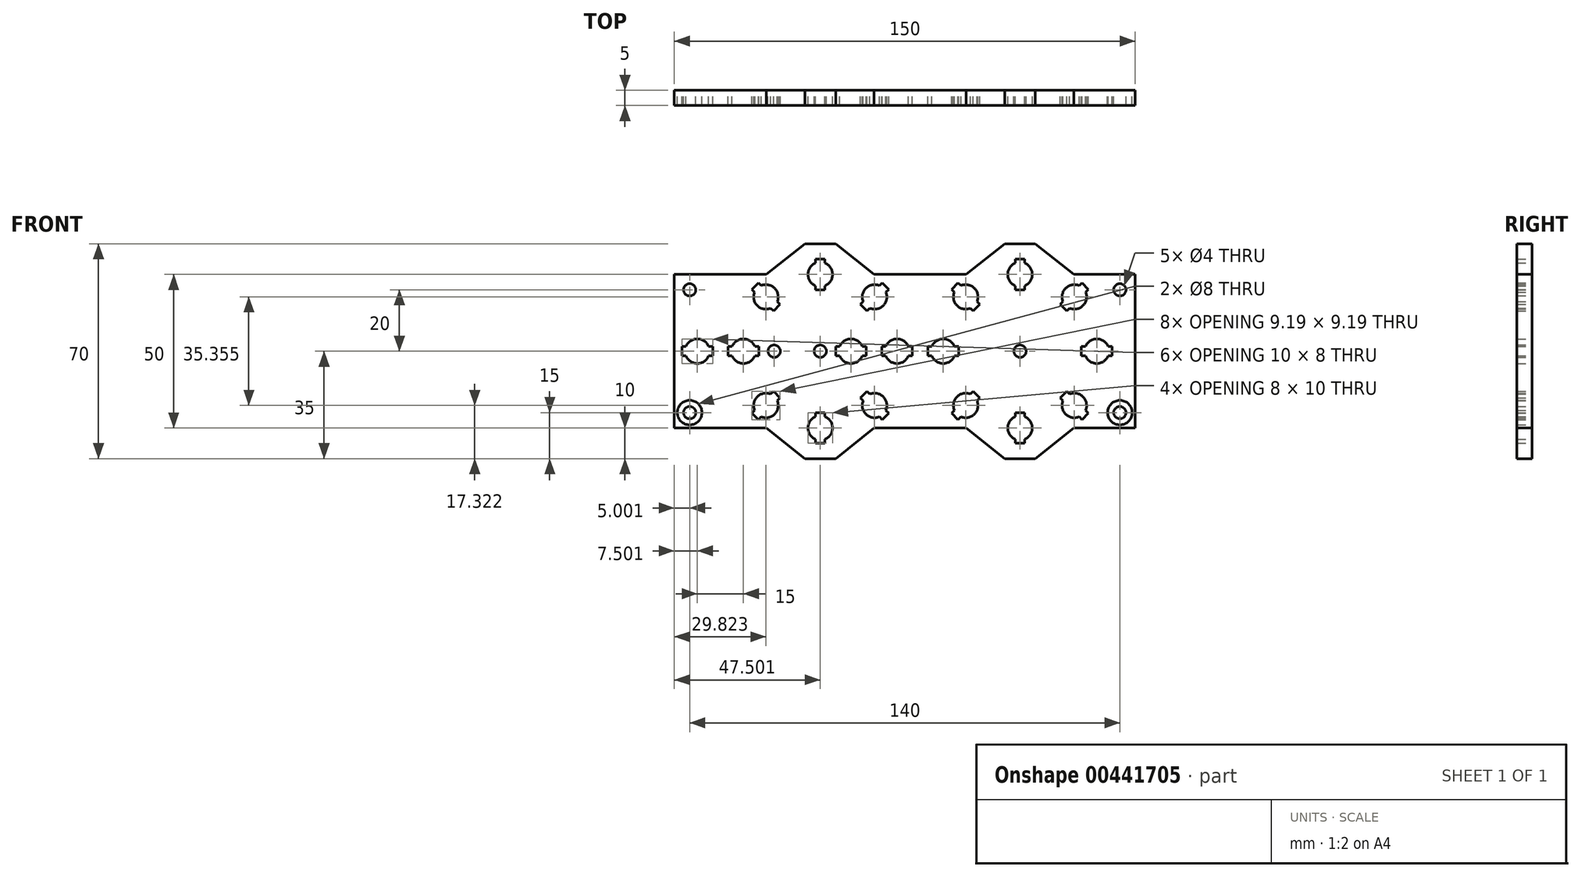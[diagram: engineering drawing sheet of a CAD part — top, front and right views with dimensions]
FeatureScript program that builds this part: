
annotation { "Feature Type Name" : "Feature", "Feature Type Description" : "" }
export const myFeature = defineFeature(function(context is Context, id is Id, definition is map)
    precondition{}
    {
        {
            var Q0;
            Q0=qCreatedBy(makeId("Front.planeOp"),FACE);
            var sketch = newSketch(context, id + "F0", { "sketchPlane" : qUnion([Q0])});
            skLineSegment(sketch, "E0", {"start": v(-68.18, 0) * mm, "end": v(-68.18, 25) * mm});
            skLineSegment(sketch, "E1", {"start": v(-68.18, 25) * mm, "end": v(-38.18, 25) * mm});
            skLineSegment(sketch, "E2", {"start": v(-38.18, 25) * mm, "end": v(-25.68, 35) * mm});
            skLineSegment(sketch, "E3", {"start": v(-25.68, 35) * mm, "end": v(-15.68, 35) * mm});
            skLineSegment(sketch, "E4", {"start": v(-15.68, 35) * mm, "end": v(-3.18, 25) * mm});
            skLineSegment(sketch, "E5", {"start": v(-3.18, 25) * mm, "end": v(26.82, 25) * mm});
            skLineSegment(sketch, "E6", {"start": v(26.82, 25) * mm, "end": v(39.32, 35) * mm});
            skLineSegment(sketch, "E7", {"start": v(39.32, 35) * mm, "end": v(49.32, 35) * mm});
            skLineSegment(sketch, "E8", {"start": v(49.32, 35) * mm, "end": v(61.82, 25) * mm});
            skLineSegment(sketch, "E9", {"start": v(61.82, 25) * mm, "end": v(81.82, 25) * mm});
            skLineSegment(sketch, "E10", {"start": v(81.82, 25) * mm, "end": v(81.82, 0) * mm});
            skLineSegment(sketch, "E11", {"start": v(-20.68, 68.45) * mm, "end": v(-20.68, -69.21) * mm, "construction": true});
            skLineSegment(sketch, "E12", {"start": v(44.32, 67.89) * mm, "end": v(44.32, -61.73) * mm, "construction": true});
            skLineSegment(sketch, "E13", {"start": v(87.46, 0) * mm, "end": v(-83.25, 0) * mm, "construction": true});
            skCircle(sketch, "E14", {"center": v(-20.68, 25) * mm, "radius": 4 * mm});
            skCircle(sketch, "E15", {"center": v(-20.68, 0) * mm, "radius": 25 * mm, "construction": true});
            skLineSegment(sketch, "E16", {"start": v(11.82, 59.27) * mm, "end": v(11.82, -51.7) * mm, "construction": true});
            skCircle(sketch, "E17.MirrorC", {"center": v(44.32, 0) * mm, "radius": 25 * mm, "construction": true});
            skCircle(sketch, "E18.MirrorC", {"center": v(44.32, 25) * mm, "radius": 4 * mm});
            skCircle(sketch, "E19.1.0", {"center": v(-38.36, 17.68) * mm, "radius": 4 * mm});
            skCircle(sketch, "E19.2.0", {"center": v(-45.68, 0) * mm, "radius": 4 * mm});
            skCircle(sketch, "E19.3.0", {"center": v(-38.36, -17.68) * mm, "radius": 4 * mm});
            skCircle(sketch, "E19.4.0", {"center": v(-20.68, -25) * mm, "radius": 4 * mm});
            skCircle(sketch, "E19.5.0", {"center": v(-3, -17.68) * mm, "radius": 4 * mm});
            skCircle(sketch, "E19.6.0", {"center": v(4.32, 0) * mm, "radius": 4 * mm});
            skCircle(sketch, "E19.7.0", {"center": v(-3, 17.68) * mm, "radius": 4 * mm});
            skCircle(sketch, "E20.MirrorC", {"center": v(62, 17.68) * mm, "radius": 4 * mm});
            skCircle(sketch, "E21.MirrorC", {"center": v(69.32, 0) * mm, "radius": 4 * mm});
            skCircle(sketch, "E22.MirrorC", {"center": v(62, -17.68) * mm, "radius": 4 * mm});
            skCircle(sketch, "E23.MirrorC", {"center": v(44.32, -25) * mm, "radius": 4 * mm});
            skCircle(sketch, "E24.MirrorC", {"center": v(26.64, -17.68) * mm, "radius": 4 * mm});
            skCircle(sketch, "E25.MirrorC", {"center": v(19.32, 0) * mm, "radius": 4 * mm});
            skCircle(sketch, "E26.MirrorC", {"center": v(26.64, 17.68) * mm, "radius": 4 * mm});
            skLineSegment(sketch, "E27.bottom", {"start": v(-22.18, 30) * mm, "end": v(-19.18, 30) * mm});
            skLineSegment(sketch, "E27.top", {"start": v(-22.18, 20) * mm, "end": v(-19.18, 20) * mm});
            skLineSegment(sketch, "E27.left", {"start": v(-22.18, 30) * mm, "end": v(-22.18, 20) * mm});
            skLineSegment(sketch, "E27.right", {"start": v(-19.18, 30) * mm, "end": v(-19.18, 20) * mm});
            skLineSegment(sketch, "E28", {"start": v(-32.15, 25) * mm, "end": v(-5.88, 25) * mm, "construction": true});
            skLineSegment(sketch, "E29.1.0", {"start": v(-42.95, 20.15) * mm, "end": v(-40.83, 22.27) * mm});
            skLineSegment(sketch, "E29.1.1", {"start": v(-42.95, 20.15) * mm, "end": v(-35.88, 13.08) * mm});
            skLineSegment(sketch, "E29.1.2", {"start": v(-35.88, 13.08) * mm, "end": v(-33.76, 15.2) * mm});
            skLineSegment(sketch, "E29.1.3", {"start": v(-40.83, 22.27) * mm, "end": v(-33.76, 15.2) * mm});
            skLineSegment(sketch, "E29.2.0", {"start": v(-50.68, -1.5) * mm, "end": v(-50.68, 1.5) * mm});
            skLineSegment(sketch, "E29.2.1", {"start": v(-50.68, -1.5) * mm, "end": v(-40.68, -1.5) * mm});
            skLineSegment(sketch, "E29.2.2", {"start": v(-40.68, -1.5) * mm, "end": v(-40.68, 1.5) * mm});
            skLineSegment(sketch, "E29.2.3", {"start": v(-50.68, 1.5) * mm, "end": v(-40.68, 1.5) * mm});
            skLineSegment(sketch, "E29.3.0", {"start": v(-40.83, -22.27) * mm, "end": v(-42.95, -20.15) * mm});
            skLineSegment(sketch, "E29.3.1", {"start": v(-40.83, -22.27) * mm, "end": v(-33.76, -15.2) * mm});
            skLineSegment(sketch, "E29.3.2", {"start": v(-33.76, -15.2) * mm, "end": v(-35.88, -13.08) * mm});
            skLineSegment(sketch, "E29.3.3", {"start": v(-42.95, -20.15) * mm, "end": v(-35.88, -13.08) * mm});
            skLineSegment(sketch, "E29.4.0", {"start": v(-19.18, -30) * mm, "end": v(-22.18, -30) * mm});
            skLineSegment(sketch, "E29.4.1", {"start": v(-19.18, -30) * mm, "end": v(-19.18, -20) * mm});
            skLineSegment(sketch, "E29.4.2", {"start": v(-19.18, -20) * mm, "end": v(-22.18, -20) * mm});
            skLineSegment(sketch, "E29.4.3", {"start": v(-22.18, -30) * mm, "end": v(-22.18, -20) * mm});
            skLineSegment(sketch, "E29.5.0", {"start": v(1.6, -20.15) * mm, "end": v(-0.53, -22.27) * mm});
            skLineSegment(sketch, "E29.5.1", {"start": v(1.6, -20.15) * mm, "end": v(-5.48, -13.08) * mm});
            skLineSegment(sketch, "E29.5.2", {"start": v(-5.48, -13.08) * mm, "end": v(-7.6, -15.2) * mm});
            skLineSegment(sketch, "E29.5.3", {"start": v(-0.53, -22.27) * mm, "end": v(-7.6, -15.2) * mm});
            skLineSegment(sketch, "E29.6.0", {"start": v(9.32, 1.5) * mm, "end": v(9.32, -1.5) * mm});
            skLineSegment(sketch, "E29.6.1", {"start": v(9.32, 1.5) * mm, "end": v(-0.68, 1.5) * mm});
            skLineSegment(sketch, "E29.6.2", {"start": v(-0.68, 1.5) * mm, "end": v(-0.68, -1.5) * mm});
            skLineSegment(sketch, "E29.6.3", {"start": v(9.32, -1.5) * mm, "end": v(-0.68, -1.5) * mm});
            skLineSegment(sketch, "E29.7.0", {"start": v(-0.53, 22.27) * mm, "end": v(1.6, 20.15) * mm});
            skLineSegment(sketch, "E29.7.1", {"start": v(-0.53, 22.27) * mm, "end": v(-7.6, 15.2) * mm});
            skLineSegment(sketch, "E29.7.2", {"start": v(-7.6, 15.2) * mm, "end": v(-5.48, 13.08) * mm});
            skLineSegment(sketch, "E29.7.3", {"start": v(1.6, 20.15) * mm, "end": v(-5.48, 13.08) * mm});
            skLineSegment(sketch, "E30.MirrorCS", {"start": v(45.82, 30) * mm, "end": v(42.82, 30) * mm});
            skLineSegment(sketch, "E31.MirrorCS", {"start": v(45.82, 30) * mm, "end": v(45.82, 20) * mm});
            skLineSegment(sketch, "E32.MirrorCS", {"start": v(45.82, 20) * mm, "end": v(42.82, 20) * mm});
            skLineSegment(sketch, "E33.MirrorCS", {"start": v(42.82, 30) * mm, "end": v(42.82, 20) * mm});
            skLineSegment(sketch, "E34.MirrorCS", {"start": v(24.17, 22.27) * mm, "end": v(31.24, 15.2) * mm});
            skLineSegment(sketch, "E35.MirrorCS", {"start": v(22.05, 20.15) * mm, "end": v(29.12, 13.08) * mm});
            skLineSegment(sketch, "E36.MirrorCS", {"start": v(31.24, 15.2) * mm, "end": v(29.12, 13.08) * mm});
            skLineSegment(sketch, "E37.MirrorCS", {"start": v(24.17, 22.27) * mm, "end": v(22.05, 20.15) * mm});
            skLineSegment(sketch, "E38.MirrorCS", {"start": v(-68.18, 0) * mm, "end": v(-68.18, -25) * mm});
            skLineSegment(sketch, "E39.MirrorCS", {"start": v(-68.18, -25) * mm, "end": v(-38.18, -25) * mm});
            skLineSegment(sketch, "E40.MirrorCS", {"start": v(-38.18, -25) * mm, "end": v(-25.68, -35) * mm});
            skLineSegment(sketch, "E41.MirrorCS", {"start": v(-25.68, -35) * mm, "end": v(-15.68, -35) * mm});
            skLineSegment(sketch, "E42.MirrorCS", {"start": v(-15.68, -35) * mm, "end": v(-3.18, -25) * mm});
            skLineSegment(sketch, "E43.MirrorCS", {"start": v(-3.18, -25) * mm, "end": v(26.82, -25) * mm});
            skLineSegment(sketch, "E44.MirrorCS", {"start": v(26.82, -25) * mm, "end": v(39.32, -35) * mm});
            skLineSegment(sketch, "E45.MirrorCS", {"start": v(39.32, -35) * mm, "end": v(49.32, -35) * mm});
            skLineSegment(sketch, "E46.MirrorCS", {"start": v(49.32, -35) * mm, "end": v(61.82, -25) * mm});
            skLineSegment(sketch, "E47.MirrorCS", {"start": v(61.82, -25) * mm, "end": v(81.82, -25) * mm});
            skLineSegment(sketch, "E48.MirrorCS", {"start": v(81.82, -25) * mm, "end": v(81.82, 0) * mm});
            skLineSegment(sketch, "E49.MirrorCS", {"start": v(14.32, 1.5) * mm, "end": v(24.32, 1.5) * mm});
            skLineSegment(sketch, "E50.MirrorCS", {"start": v(14.32, -1.5) * mm, "end": v(24.32, -1.5) * mm});
            skLineSegment(sketch, "E51.MirrorCS", {"start": v(14.32, 1.5) * mm, "end": v(14.32, -1.5) * mm});
            skLineSegment(sketch, "E52.MirrorCS", {"start": v(24.32, 1.5) * mm, "end": v(24.32, -1.5) * mm});
            skLineSegment(sketch, "E53.MirrorCS", {"start": v(29.12, -13.08) * mm, "end": v(31.24, -15.2) * mm});
            skLineSegment(sketch, "E54.MirrorCS", {"start": v(24.17, -22.27) * mm, "end": v(31.24, -15.2) * mm});
            skLineSegment(sketch, "E55.MirrorCS", {"start": v(22.05, -20.15) * mm, "end": v(29.12, -13.08) * mm});
            skLineSegment(sketch, "E56.MirrorCS", {"start": v(22.05, -20.15) * mm, "end": v(24.17, -22.27) * mm});
            skLineSegment(sketch, "E57.MirrorCS", {"start": v(42.82, -30) * mm, "end": v(45.82, -30) * mm});
            skLineSegment(sketch, "E58.MirrorCS", {"start": v(45.82, -30) * mm, "end": v(45.82, -20) * mm});
            skLineSegment(sketch, "E59.MirrorCS", {"start": v(42.82, -20) * mm, "end": v(45.82, -20) * mm});
            skLineSegment(sketch, "E60.MirrorCS", {"start": v(42.82, -30) * mm, "end": v(42.82, -20) * mm});
            skLineSegment(sketch, "E61.MirrorCS", {"start": v(64.47, -22.27) * mm, "end": v(57.4, -15.2) * mm});
            skLineSegment(sketch, "E62.MirrorCS", {"start": v(66.6, -20.15) * mm, "end": v(59.52, -13.08) * mm});
            skLineSegment(sketch, "E63.MirrorCS", {"start": v(64.47, -22.27) * mm, "end": v(66.6, -20.15) * mm});
            skLineSegment(sketch, "E64.MirrorCS", {"start": v(57.4, -15.2) * mm, "end": v(59.52, -13.08) * mm});
            skLineSegment(sketch, "E65.MirrorCS", {"start": v(74.32, -1.5) * mm, "end": v(64.32, -1.5) * mm});
            skLineSegment(sketch, "E66.MirrorCS", {"start": v(74.32, 1.5) * mm, "end": v(64.32, 1.5) * mm});
            skLineSegment(sketch, "E67.MirrorCS", {"start": v(64.32, -1.5) * mm, "end": v(64.32, 1.5) * mm});
            skLineSegment(sketch, "E68.MirrorCS", {"start": v(74.32, -1.5) * mm, "end": v(74.32, 1.5) * mm});
            skLineSegment(sketch, "E69.MirrorCS", {"start": v(59.52, 13.08) * mm, "end": v(57.4, 15.2) * mm});
            skLineSegment(sketch, "E70.MirrorCS", {"start": v(64.47, 22.27) * mm, "end": v(57.4, 15.2) * mm});
            skLineSegment(sketch, "E71.MirrorCS", {"start": v(66.6, 20.15) * mm, "end": v(59.52, 13.08) * mm});
            skLineSegment(sketch, "E72.MirrorCS", {"start": v(66.6, 20.15) * mm, "end": v(64.47, 22.27) * mm});
            skCircle(sketch, "E73", {"center": v(-20.68, 0) * mm, "radius": 2 * mm});
            skCircle(sketch, "E74.MirrorC", {"center": v(44.32, 0) * mm, "radius": 2 * mm});
            skCircle(sketch, "E75", {"center": v(-35.68, 0) * mm, "radius": 2 * mm});
            skCircle(sketch, "E76.2.0", {"center": v(-60.68, 0) * mm, "radius": 4 * mm});
            skLineSegment(sketch, "E77.2.0", {"start": v(-65.68, -1.5) * mm, "end": v(-65.68, 1.5) * mm});
            skLineSegment(sketch, "E77.2.1", {"start": v(-65.68, -1.5) * mm, "end": v(-55.68, -1.5) * mm});
            skLineSegment(sketch, "E77.2.2", {"start": v(-55.68, -1.5) * mm, "end": v(-55.68, 1.5) * mm});
            skLineSegment(sketch, "E77.2.3", {"start": v(-65.68, 1.5) * mm, "end": v(-55.68, 1.5) * mm});
            skLineSegment(sketch, "E78", {"start": v(-60.68, 7.22) * mm, "end": v(-60.68, -6.04) * mm, "construction": true});
            skLineSegment(sketch, "E79", {"start": v(-35.68, 4.02) * mm, "end": v(-35.68, -7.57) * mm, "construction": true});
            skCircle(sketch, "E80.MirrorC", {"center": v(-10.68, 0) * mm, "radius": 4 * mm});
            skLineSegment(sketch, "E81.MirrorCS", {"start": v(-5.68, 1.5) * mm, "end": v(-15.68, 1.5) * mm});
            skLineSegment(sketch, "E82.MirrorCS", {"start": v(-5.68, -1.5) * mm, "end": v(-15.68, -1.5) * mm});
            skLineSegment(sketch, "E83.MirrorCS", {"start": v(-15.68, -1.5) * mm, "end": v(-15.68, 1.5) * mm});
            skLineSegment(sketch, "E84.MirrorCS", {"start": v(-5.68, -1.5) * mm, "end": v(-5.68, 1.5) * mm});
            skLineSegment(sketch, "E85.MirrorCS", {"start": v(-10.68, 7.22) * mm, "end": v(-10.68, -6.04) * mm, "construction": true});
            skSolve(sketch);
        }
        {
            var Q0;
            Q0=qSketchRegion(id+"F0",true);
            extrude(context, id + "F1", {"entities" : qUnion([Q0]), "endBound" : BoundingType.SYMMETRIC, "depth" : 5 * mm});
        }
        {
            var Q0;
            Q0=makeQuery(id+"F1.opExtrude","CAP_FACE",FACE,{"disambiguationData":[OSD([sQuery(id+"F0.wireOp",EDGE,"E0"),sQuery(id+"F0.wireOp",EDGE,"E1"),sQuery(id+"F0.wireOp",EDGE,"E2"),sQuery(id+"F0.wireOp",EDGE,"E3"),sQuery(id+"F0.wireOp",EDGE,"E4"),sQuery(id+"F0.wireOp",EDGE,"E5"),sQuery(id+"F0.wireOp",EDGE,"E6"),sQuery(id+"F0.wireOp",EDGE,"E7"),sQuery(id+"F0.wireOp",EDGE,"E8"),sQuery(id+"F0.wireOp",EDGE,"E9"),sQuery(id+"F0.wireOp",EDGE,"E10"),sQuery(id+"F0.wireOp",EDGE,"E14"),sQuery(id+"F0.wireOp",EDGE,"E18.MirrorC"),sQuery(id+"F0.wireOp",EDGE,"E19.1.0"),sQuery(id+"F0.wireOp",EDGE,"E19.2.0"),sQuery(id+"F0.wireOp",EDGE,"E19.3.0"),sQuery(id+"F0.wireOp",EDGE,"E19.4.0"),sQuery(id+"F0.wireOp",EDGE,"E19.5.0"),sQuery(id+"F0.wireOp",EDGE,"E19.6.0"),sQuery(id+"F0.wireOp",EDGE,"E19.7.0"),sQuery(id+"F0.wireOp",EDGE,"E20.MirrorC"),sQuery(id+"F0.wireOp",EDGE,"E21.MirrorC"),sQuery(id+"F0.wireOp",EDGE,"E22.MirrorC"),sQuery(id+"F0.wireOp",EDGE,"E23.MirrorC"),sQuery(id+"F0.wireOp",EDGE,"E24.MirrorC"),sQuery(id+"F0.wireOp",EDGE,"E25.MirrorC"),sQuery(id+"F0.wireOp",EDGE,"E26.MirrorC"),sQuery(id+"F0.wireOp",EDGE,"E27.bottom"),sQuery(id+"F0.wireOp",EDGE,"E27.top"),sQuery(id+"F0.wireOp",EDGE,"E27.left"),sQuery(id+"F0.wireOp",EDGE,"E27.right"),sQuery(id+"F0.wireOp",EDGE,"E29.1.0"),sQuery(id+"F0.wireOp",EDGE,"E29.1.1"),sQuery(id+"F0.wireOp",EDGE,"E29.1.2"),sQuery(id+"F0.wireOp",EDGE,"E29.1.3"),sQuery(id+"F0.wireOp",EDGE,"E29.2.0"),sQuery(id+"F0.wireOp",EDGE,"E29.2.1"),sQuery(id+"F0.wireOp",EDGE,"E29.2.2"),sQuery(id+"F0.wireOp",EDGE,"E29.2.3"),sQuery(id+"F0.wireOp",EDGE,"E29.3.0"),sQuery(id+"F0.wireOp",EDGE,"E29.3.1"),sQuery(id+"F0.wireOp",EDGE,"E29.3.2"),sQuery(id+"F0.wireOp",EDGE,"E29.3.3"),sQuery(id+"F0.wireOp",EDGE,"E29.4.0"),sQuery(id+"F0.wireOp",EDGE,"E29.4.1"),sQuery(id+"F0.wireOp",EDGE,"E29.4.2"),sQuery(id+"F0.wireOp",EDGE,"E29.4.3"),sQuery(id+"F0.wireOp",EDGE,"E29.5.0"),sQuery(id+"F0.wireOp",EDGE,"E29.5.1"),sQuery(id+"F0.wireOp",EDGE,"E29.5.2"),sQuery(id+"F0.wireOp",EDGE,"E29.5.3"),sQuery(id+"F0.wireOp",EDGE,"E29.6.0"),sQuery(id+"F0.wireOp",EDGE,"E29.6.1"),sQuery(id+"F0.wireOp",EDGE,"E29.6.2"),sQuery(id+"F0.wireOp",EDGE,"E29.6.3"),sQuery(id+"F0.wireOp",EDGE,"E29.7.0"),sQuery(id+"F0.wireOp",EDGE,"E29.7.1"),sQuery(id+"F0.wireOp",EDGE,"E29.7.2"),sQuery(id+"F0.wireOp",EDGE,"E29.7.3"),sQuery(id+"F0.wireOp",EDGE,"E30.MirrorCS"),sQuery(id+"F0.wireOp",EDGE,"E31.MirrorCS"),sQuery(id+"F0.wireOp",EDGE,"E32.MirrorCS"),sQuery(id+"F0.wireOp",EDGE,"E33.MirrorCS"),sQuery(id+"F0.wireOp",EDGE,"E34.MirrorCS"),sQuery(id+"F0.wireOp",EDGE,"E35.MirrorCS"),sQuery(id+"F0.wireOp",EDGE,"E36.MirrorCS"),sQuery(id+"F0.wireOp",EDGE,"E37.MirrorCS"),sQuery(id+"F0.wireOp",EDGE,"E38.MirrorCS"),sQuery(id+"F0.wireOp",EDGE,"E39.MirrorCS"),sQuery(id+"F0.wireOp",EDGE,"E40.MirrorCS"),sQuery(id+"F0.wireOp",EDGE,"E41.MirrorCS"),sQuery(id+"F0.wireOp",EDGE,"E42.MirrorCS"),sQuery(id+"F0.wireOp",EDGE,"E43.MirrorCS"),sQuery(id+"F0.wireOp",EDGE,"E44.MirrorCS"),sQuery(id+"F0.wireOp",EDGE,"E45.MirrorCS"),sQuery(id+"F0.wireOp",EDGE,"E46.MirrorCS"),sQuery(id+"F0.wireOp",EDGE,"E47.MirrorCS"),sQuery(id+"F0.wireOp",EDGE,"E48.MirrorCS"),sQuery(id+"F0.wireOp",EDGE,"E49.MirrorCS"),sQuery(id+"F0.wireOp",EDGE,"E50.MirrorCS"),sQuery(id+"F0.wireOp",EDGE,"E51.MirrorCS"),sQuery(id+"F0.wireOp",EDGE,"E52.MirrorCS"),sQuery(id+"F0.wireOp",EDGE,"E53.MirrorCS"),sQuery(id+"F0.wireOp",EDGE,"E54.MirrorCS"),sQuery(id+"F0.wireOp",EDGE,"E55.MirrorCS"),sQuery(id+"F0.wireOp",EDGE,"E56.MirrorCS"),sQuery(id+"F0.wireOp",EDGE,"E57.MirrorCS"),sQuery(id+"F0.wireOp",EDGE,"E58.MirrorCS"),sQuery(id+"F0.wireOp",EDGE,"E59.MirrorCS"),sQuery(id+"F0.wireOp",EDGE,"E60.MirrorCS"),sQuery(id+"F0.wireOp",EDGE,"E61.MirrorCS"),sQuery(id+"F0.wireOp",EDGE,"E62.MirrorCS"),sQuery(id+"F0.wireOp",EDGE,"E63.MirrorCS"),sQuery(id+"F0.wireOp",EDGE,"E64.MirrorCS"),sQuery(id+"F0.wireOp",EDGE,"E65.MirrorCS"),sQuery(id+"F0.wireOp",EDGE,"E66.MirrorCS"),sQuery(id+"F0.wireOp",EDGE,"E67.MirrorCS"),sQuery(id+"F0.wireOp",EDGE,"E68.MirrorCS"),sQuery(id+"F0.wireOp",EDGE,"E69.MirrorCS"),sQuery(id+"F0.wireOp",EDGE,"E70.MirrorCS"),sQuery(id+"F0.wireOp",EDGE,"E71.MirrorCS"),sQuery(id+"F0.wireOp",EDGE,"E72.MirrorCS"),sQuery(id+"F0.wireOp",EDGE,"E73"),sQuery(id+"F0.wireOp",EDGE,"E74.MirrorC")])],"isStart":true});
            var sketch = newSketch(context, id + "F2", { "sketchPlane" : qUnion([Q0])});
            skCircle(sketch, "E86", {"center": v(-76.82, 20) * mm, "radius": 4 * mm});
            skCircle(sketch, "E87", {"center": v(-76.82, 20) * mm, "radius": 2 * mm});
            skLineSegment(sketch, "E88", {"start": v(-96.16, 0) * mm, "end": v(117.4, 0) * mm, "construction": true});
            skCircle(sketch, "E89.MirrorC", {"center": v(-76.82, -20) * mm, "radius": 4 * mm});
            skCircle(sketch, "E90.MirrorC", {"center": v(-76.82, -20) * mm, "radius": 2 * mm});
            skCircle(sketch, "E91", {"center": v(63.18, 20) * mm, "radius": 2 * mm});
            skCircle(sketch, "E92", {"center": v(63.18, 20) * mm, "radius": 4 * mm});
            skCircle(sketch, "E93.MirrorC", {"center": v(63.18, -20) * mm, "radius": 4 * mm});
            skCircle(sketch, "E94.MirrorC", {"center": v(63.18, -20) * mm, "radius": 2 * mm});
            skSolve(sketch);
        }
        {
            var Q0;
            Q0=makeQuery(id+"F2.imprint","IMPRINT",FACE,{"disambiguationData":[TD([[makeQuery(id+"F2.imprint","IMPRINT",EDGE,{"derivedFrom":sQuery(id+"F2.wireOp",EDGE,"E87")}),1.0]])]});
            var Q1;
            Q1=makeQuery(id+"F2.imprint","IMPRINT",FACE,{"disambiguationData":[TD([[makeQuery(id+"F2.imprint","IMPRINT",EDGE,{"derivedFrom":sQuery(id+"F2.wireOp",EDGE,"E90.MirrorC")}),-1.0]])]});
            var Q2;
            Q2=makeQuery(id+"F2.imprint","IMPRINT",FACE,{"disambiguationData":[TD([[makeQuery(id+"F2.imprint","IMPRINT",EDGE,{"derivedFrom":sQuery(id+"F2.wireOp",EDGE,"E91")}),1.0]])]});
            var Q3;
            Q3=makeQuery(id+"F2.imprint","IMPRINT",FACE,{"disambiguationData":[TD([[makeQuery(id+"F2.imprint","IMPRINT",EDGE,{"derivedFrom":sQuery(id+"F2.wireOp",EDGE,"E94.MirrorC")}),-1.0]])]});
            extrude(context, id + "F3", {"entities" : qUnion([Q0, Q1, Q2, Q3]), "operationType" : NewBodyOperationType.REMOVE, "endBound" : BoundingType.THROUGH_ALL, "oppositeDirection" : true, "depth" : 25 * mm});
        }
    });
